# Revit family: Vollrath_60039
name_source: partatom
category: Specialty Equipment
units: mm (PartAtom-declared; Revit-internal decimal feet)

## family parameters
Always vertical = No
Cut with Voids When Loaded = No
OmniClass Number = 23.40.40.00
OmniClass Title = Food Service Equipment and Furnishings
Part Type = Normal
Room Calculation Point = No
Round Connector Dimension = Use Diameter
Shared = Yes
Work Plane-Based = Yes

## types (1)
- Vollrath_60039
    Apparent Power = 1440 VA
    Cold Water Connection Height = 0 "
    Cold Water Consumption = 0
    Cold Water Flow = 0 GPM
    Cold Water Maximum Pressure = 0.00 psi
    Cold Water Minimum Pressure = 0.00 psi
    Cold Water Size = 0"
    Cold Water Temperature Recommended = 0 °F
    Conn Conduit = Yes
    Conn Plug = NEMA 5-15p
    Cycle = 60 Hz
    Default Elevation = 48 "
    Description = 120 IMMERS CIRC W/BATH & COVER
    Elec Conn Connection Height = 0 "
    FL Amps = 12 A
    Foodservice Equipment Identifier = Yes
    IsLegacy_Config = 0
    IsLegacy_Custom = 0
    Manufacturer = Vollrath
    Max Overcurrent Protection = 0 A
    Min Ckt Ampacity = 0 A
    PartNo_Config = 40861
    PartNo_Custom = 60039
    Phase = 1
    Redraw_Config = 0
    Redraw_Custom = 0
    Volts = 120 V
    Watts = 1500 W
    Weight in Pounds = 49

## geometry (parser evidence)
native form markers: Blend x4, Sweep x26
no freeform markers — native parametric forms only
